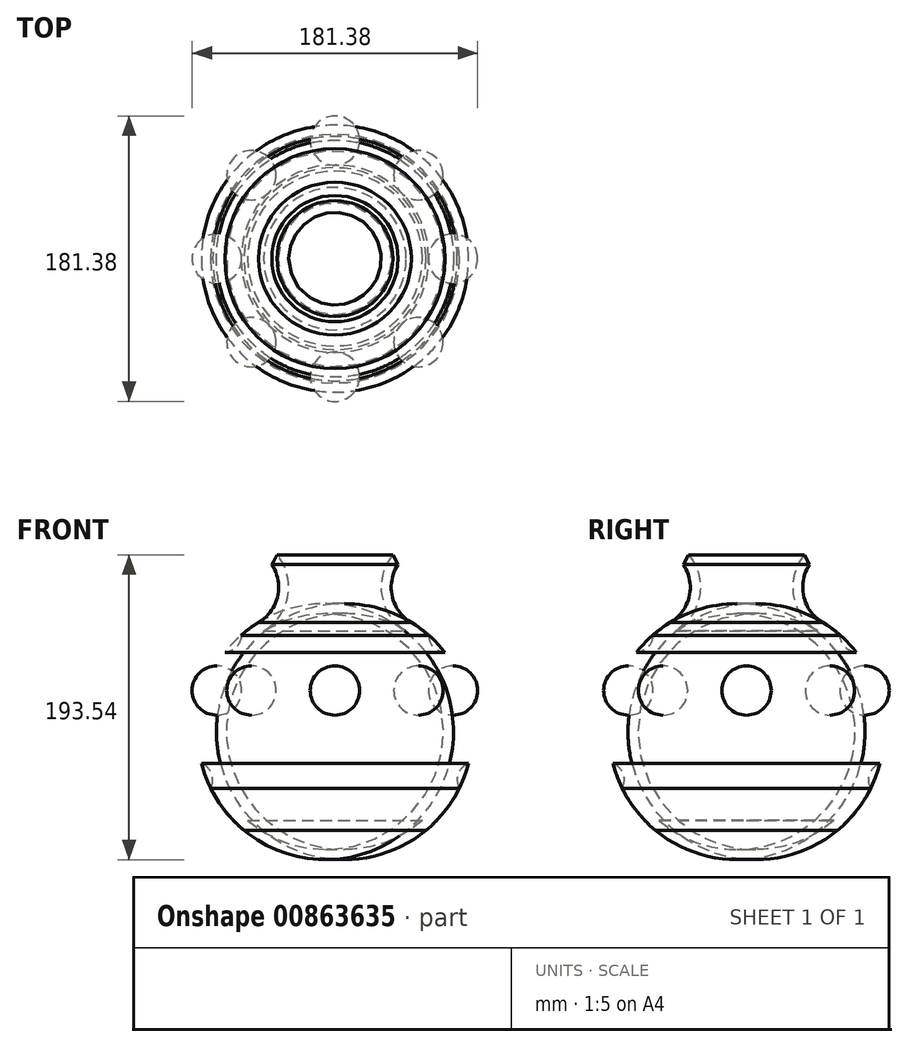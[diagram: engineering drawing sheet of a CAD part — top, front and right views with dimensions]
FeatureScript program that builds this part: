
annotation { "Feature Type Name" : "Feature", "Feature Type Description" : "" }
export const myFeature = defineFeature(function(context is Context, id is Id, definition is map)
    precondition{}
    {
        {
            var Q0;
            Q0=qCreatedBy(makeId("Front.planeOp"),FACE);
            var sketch = newSketch(context, id + "F0", { "sketchPlane" : qUnion([Q0])});
            skLineSegment(sketch, "E0", {"start": v(0, 0) * mm, "end": v(0, 176.63) * mm});
            skLineSegment(sketch, "E1", {"start": v(0, 176.63) * mm, "end": v(48.5, 176.63) * mm});
            skLineSegment(sketch, "E2", {"start": v(0, 0) * mm, "end": v(57.83, 0) * mm});
            skArc(sketch, "E3", {"start": v(48.5, 176.63) * mm, "mid": v(35.7, 154.31) * mm, "end": v(48.5, 132) * mm});
            skArc(sketch, "E4", {"start": v(57.83, 0) * mm, "mid": v(87.13, 68.4) * mm, "end": v(48.5, 132) * mm});
            skSolve(sketch);
        }
        {
            var Q0;
            Q0=makeQuery(id+"F0.imprint","IMPRINT",FACE,{"disambiguationData":[TD([[makeQuery(id+"F0.imprint","IMPRINT",EDGE,{"derivedFrom":sQuery(id+"F0.wireOp",EDGE,"E0")}),-1.0]])]});
            var Q1;
            Q1=sQuery(id+"F0.wireOp",EDGE,"E0");
            revolve(context, id + "F1", {"surfaceOperationType" : NewSurfaceOperationType.NEW, "entities" : qUnion([Q0]), "axis" : qUnion([Q1]), "revolveType" : RevolveType.FULL});
        }
        {
            var Q0;
            Q0=qCreatedBy(makeId("Front.planeOp"),FACE);
            var sketch = newSketch(context, id + "F2", { "sketchPlane" : qUnion([Q0])});
            skArc(sketch, "E5", {"start": v(122.74, 91.4) * mm, "mid": v(138.44, 107.09) * mm, "end": v(122.74, 122.78) * mm});
            skLineSegment(sketch, "E6", {"start": v(122.74, 122.78) * mm, "end": v(122.74, 91.4) * mm});
            skSolve(sketch);
        }
        {
            var Q0;
            Q0=makeQuery(id+"F2.imprint","IMPRINT",FACE,{"disambiguationData":[TD([[makeQuery(id+"F2.imprint","IMPRINT",EDGE,{"derivedFrom":sQuery(id+"F2.wireOp",EDGE,"E5")}),1.0]])]});
            var Q1;
            Q1=sQuery(id+"F2.wireOp",EDGE,"E6");
            revolve(context, id + "F3", {"surfaceOperationType" : NewSurfaceOperationType.NEW, "entities" : qUnion([Q0]), "axis" : qUnion([Q1]), "revolveType" : RevolveType.FULL});
        }
        {
            var Q0;
            Q0=makeQuery(id+"F3.opRevolve","SWEPT_BODY",BODY,{"disambiguationData":[OSD([sQuery(id+"F2.wireOp",EDGE,"E5"),sQuery(id+"F2.wireOp",EDGE,"E6")])]});
            transform(context, id + "F4", {"entities" : qUnion([Q0]), "transformType" : TransformType.TRANSLATION_3D, "dx" : -47.75 * mm, "dy" : 0 * mm, "dz" : -18.29 * mm, "makeCopy" : false});
        }
        {
            var Q0;
            Q0=makeQuery(id+"F3.opRevolve","SWEPT_BODY",BODY,{"disambiguationData":[OSD([sQuery(id+"F2.wireOp",EDGE,"E5"),sQuery(id+"F2.wireOp",EDGE,"E6")])]});
            var Q1;
            Q1=makeQuery(id+"F1.opRevolve","SWEPT_EDGE",EDGE,{"disambiguationData":[OSD([sQuery(id+"F0.wireOp",EDGE,"E1"),sQuery(id+"F0.wireOp",EDGE,"E3")])]});
            circularPattern(context, id + "F5", {"entities" : qUnion([Q0]), "axis" : qUnion([Q1]), "angle" : 360 * degree, "instanceCount" : 8, "equalSpace" : true});
        }
        {
            var Q0;
            Q0=makeQuery(id+"F1.opRevolve","SWEPT_FACE",FACE,{"disambiguationData":[OSD([sQuery(id+"F0.wireOp",EDGE,"E1")])]});
            shell(context, id + "F6", {"entities" : qUnion([Q0]), "thickness" : 6.35 * mm});
        }
        {
            var Q0;
            Q0=qCreatedBy(makeId("Right.planeOp"),FACE);
            var sketch = newSketch(context, id + "F7", { "sketchPlane" : qUnion([Q0])});
            skCircle(sketch, "E7", {"center": v(-70.58, 124.05) * mm, "radius": 11.04 * mm});
            skCircle(sketch, "E8", {"center": v(-88.63, 32.09) * mm, "radius": 11.04 * mm});
            skSolve(sketch);
        }
        {
            var Q0;
            Q0=makeQuery(id+"F7.imprint","IMPRINT",FACE,{"disambiguationData":[TD([[makeQuery(id+"F7.imprint","IMPRINT",EDGE,{"derivedFrom":sQuery(id+"F7.wireOp",EDGE,"E7")}),1.0]])]});
            var Q1;
            Q1=makeQuery(id+"F7.imprint","IMPRINT",FACE,{"disambiguationData":[TD([[makeQuery(id+"F7.imprint","IMPRINT",EDGE,{"derivedFrom":sQuery(id+"F7.wireOp",EDGE,"E8")}),1.0]])]});
            var Q2;
            Q2=makeQuery(id+"F6.opShell","OFFSET_EDGE",EDGE,{"disambiguationData":[OSD([sQuery(id+"F0.wireOp",EDGE,"E1"),sQuery(id+"F0.wireOp",EDGE,"E3")])]});
            revolve(context, id + "F8", {"operationType" : NewBodyOperationType.REMOVE, "surfaceOperationType" : NewSurfaceOperationType.NEW, "entities" : qUnion([Q0, Q1]), "axis" : qUnion([Q2]), "revolveType" : RevolveType.FULL, "oppositeDirection" : true});
        }
        {
            var Q0;
            Q0=qCreatedBy(makeId("Front.planeOp"),FACE);
            var sketch = newSketch(context, id + "F9", { "sketchPlane" : qUnion([Q0])});
            skArc(sketch, "E9", {"start": v(54.12, 141.41) * mm, "mid": v(66.18, 153.47) * mm, "end": v(54.12, 165.53) * mm});
            skLineSegment(sketch, "E10", {"start": v(54.12, 165.53) * mm, "end": v(54.12, 141.41) * mm});
            skSolve(sketch);
        }
        {
            var Q0;
            Q0=makeQuery(id+"F9.imprint","IMPRINT",FACE,{"disambiguationData":[TD([[makeQuery(id+"F9.imprint","IMPRINT",EDGE,{"derivedFrom":sQuery(id+"F9.wireOp",EDGE,"E9")}),1.0]])]});
            var Q1;
            Q1=sQuery(id+"F9.wireOp",EDGE,"E10");
            revolve(context, id + "F10", {"surfaceOperationType" : NewSurfaceOperationType.NEW, "entities" : qUnion([Q0]), "axis" : qUnion([Q1]), "revolveType" : RevolveType.FULL});
        }
        {
            var Q0;
            Q0=makeQuery(id+"F10.opRevolve","SWEPT_BODY",BODY,{"disambiguationData":[OSD([sQuery(id+"F9.wireOp",EDGE,"E9"),sQuery(id+"F9.wireOp",EDGE,"E10")])]});
            transform(context, id + "F11", {"entities" : qUnion([Q0]), "transformType" : TransformType.TRANSLATION_3D, "dx" : -20.83 * mm, "dy" : 0 * mm, "dz" : 0 * mm, "makeCopy" : false});
        }
        {
            var Q0;
            Q0=makeQuery(id+"F10.opRevolve","SWEPT_BODY",BODY,{"disambiguationData":[OSD([sQuery(id+"F9.wireOp",EDGE,"E9"),sQuery(id+"F9.wireOp",EDGE,"E10")])]});
            var Q1;
            Q1=makeQuery(id+"F6.opShell","OFFSET_EDGE",EDGE,{"disambiguationData":[OSD([sQuery(id+"F0.wireOp",EDGE,"E1"),sQuery(id+"F0.wireOp",EDGE,"E3")])]});
            circularPattern(context, id + "F12", {"entities" : qUnion([Q0]), "axis" : qUnion([Q1]), "angle" : 360 * degree, "instanceCount" : 6, "equalSpace" : true});
        }
        {
            var Q0;
            Q0=makeQuery(id+"F12.opPattern","COPY",BODY,{"derivedFrom":makeQuery(id+"F10.opRevolve","SWEPT_BODY",BODY,{"disambiguationData":[OSD([sQuery(id+"F9.wireOp",EDGE,"E9"),sQuery(id+"F9.wireOp",EDGE,"E10")])]}),"instanceName":"2"});
            var Q1;
            Q1=makeQuery(id+"F12.opPattern","COPY",BODY,{"derivedFrom":makeQuery(id+"F10.opRevolve","SWEPT_BODY",BODY,{"disambiguationData":[OSD([sQuery(id+"F9.wireOp",EDGE,"E9"),sQuery(id+"F9.wireOp",EDGE,"E10")])]}),"instanceName":"3"});
            var Q2;
            Q2=makeQuery(id+"F12.opPattern","COPY",BODY,{"derivedFrom":makeQuery(id+"F10.opRevolve","SWEPT_BODY",BODY,{"disambiguationData":[OSD([sQuery(id+"F9.wireOp",EDGE,"E9"),sQuery(id+"F9.wireOp",EDGE,"E10")])]}),"instanceName":"4"});
            var Q3;
            Q3=makeQuery(id+"F12.opPattern","COPY",BODY,{"derivedFrom":makeQuery(id+"F10.opRevolve","SWEPT_BODY",BODY,{"disambiguationData":[OSD([sQuery(id+"F9.wireOp",EDGE,"E9"),sQuery(id+"F9.wireOp",EDGE,"E10")])]}),"instanceName":"5"});
            var Q4;
            Q4=makeQuery(id+"F10.opRevolve","SWEPT_BODY",BODY,{"disambiguationData":[OSD([sQuery(id+"F9.wireOp",EDGE,"E9"),sQuery(id+"F9.wireOp",EDGE,"E10")])]});
            var Q5;
            Q5=makeQuery(id+"F12.opPattern","COPY",BODY,{"derivedFrom":makeQuery(id+"F10.opRevolve","SWEPT_BODY",BODY,{"disambiguationData":[OSD([sQuery(id+"F9.wireOp",EDGE,"E9"),sQuery(id+"F9.wireOp",EDGE,"E10")])]}),"instanceName":"1"});
            var Q6;
            Q6=makeQuery(id+"F5.opPattern","COPY",BODY,{"derivedFrom":makeQuery(id+"F3.opRevolve","SWEPT_BODY",BODY,{"disambiguationData":[OSD([sQuery(id+"F2.wireOp",EDGE,"E5"),sQuery(id+"F2.wireOp",EDGE,"E6")])]}),"instanceName":"5"});
            booleanBodies(context, id + "F13", {"operationType" : BooleanOperationType.SUBTRACTION, "tools" : qUnion([Q0, Q1, Q2, Q3, Q4, Q5]), "targets" : qUnion([Q6])});
        }
        {
            var Q0;
            Q0=makeQuery(id+"F1.opRevolve","SWEPT_EDGE",EDGE,{"disambiguationData":[OSD([sQuery(id+"F0.wireOp",EDGE,"E1"),sQuery(id+"F0.wireOp",EDGE,"E3")])]});
            chamfer(context, id + "F14", {"entities" : qUnion([Q0]), "width" : 5.08 * mm, "tangentPropagation" : true});
        }
    });
